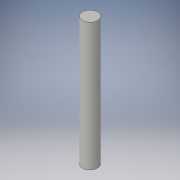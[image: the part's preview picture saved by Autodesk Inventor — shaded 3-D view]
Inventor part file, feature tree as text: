
AUTODESK INVENTOR PART (.ipt)
format: ipt  version: 2016 (Build 200138000, 138)  size: 84,992 bytes
history: native  units: in
note: dims shown in document units (in); Inventor stores cm internally (conversion verified against a paired STEP export)
features: extrude x1, sketch x1
ambient origin geometry x8: Origin, YZ Plane, XZ Plane, XY Plane, X Axis, Y Axis, Z Axis, Center Point
bodies: Solid1 (feature_tree)
feature tree (2):
  extrude  "Extrusion1"  Depth=1.6in TaperAngle=0.0deg
  sketch  "Sketch1"  dims[d0=0.188in d1=1.6in d2=0.0in]
